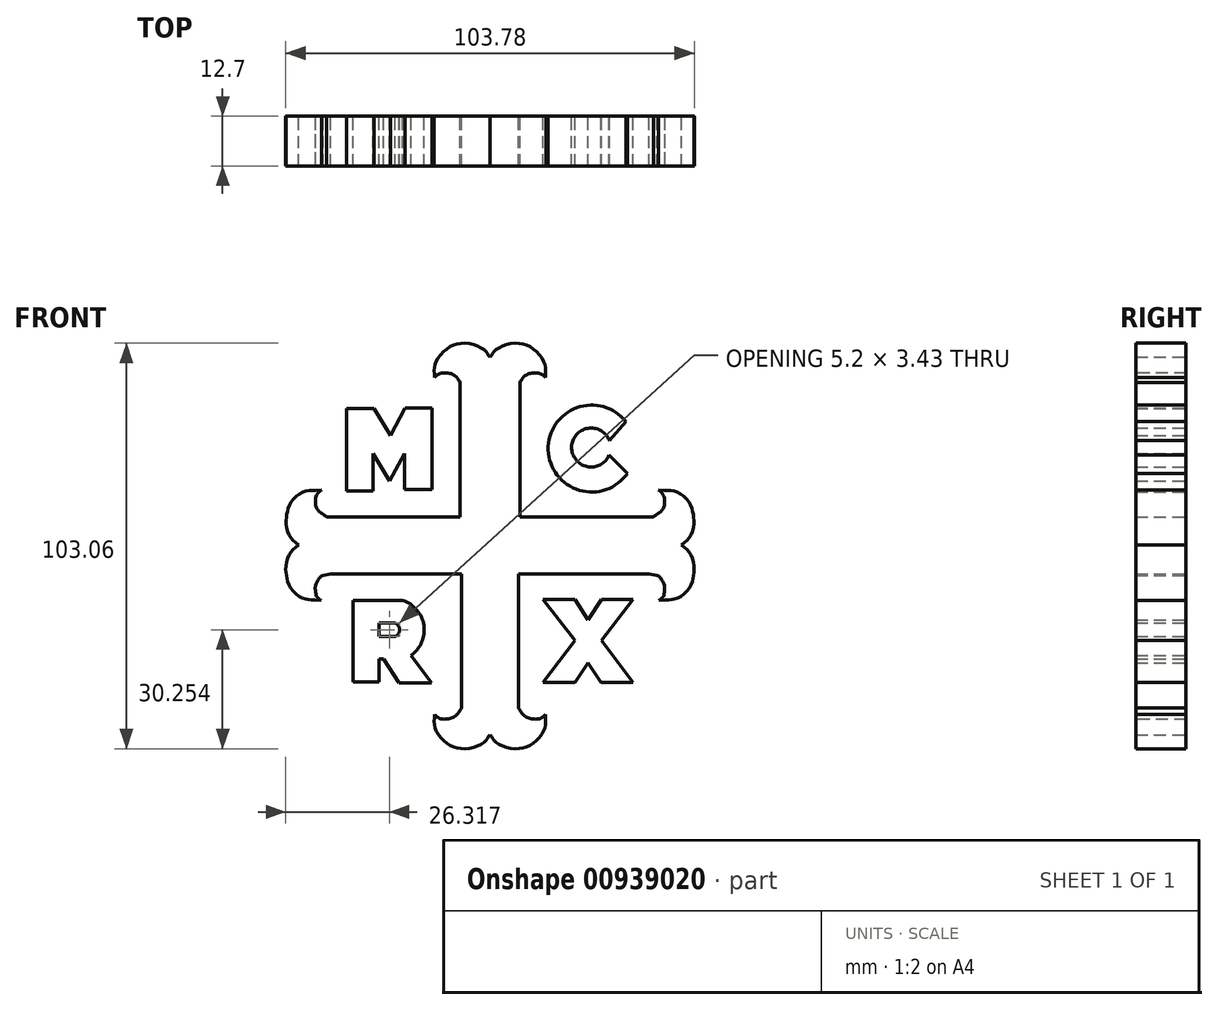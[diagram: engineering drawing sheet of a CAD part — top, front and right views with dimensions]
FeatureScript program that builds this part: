
annotation { "Feature Type Name" : "Feature", "Feature Type Description" : "" }
export const myFeature = defineFeature(function(context is Context, id is Id, definition is map)
    precondition{}
    {
        {
            var Q0;
            Q0=qCreatedBy(makeId("Front.planeOp"),FACE);
            var sketch = newSketch(context, id + "F0", { "sketchPlane" : qUnion([Q0])});
            skFitSpline(sketch, "E0", {"points": [v(0, 47.98) * mm, v(-0.62, 48.8) * mm, v(-1.48, 49.84) * mm, v(-4.4, 51.28) * mm, v(-8.19, 51.36) * mm, v(-10.9, 50.16) * mm, v(-13.4, 47.4) * mm, v(-14.12, 45.3) * mm, v(-14.12, 42.79) * mm], "startDerivative": vector(-12.73, 4.5) * mm, "endDerivative": vector(1.03, -20.51) * mm});
            skFitSpline(sketch, "E1", {"points": [v(-14.12, 42.79) * mm, v(-12.86, 43.77) * mm, v(-11.23, 44) * mm, v(-9.01, 43.33) * mm, v(-7.6, 41.55) * mm], "startDerivative": vector(4.45, 4.62) * mm, "endDerivative": vector(4.3, -7.5) * mm});
            skLineSegment(sketch, "E2", {"start": v(-7.6, 41.55) * mm, "end": v(-7.6, 7.35) * mm});
            skLineSegment(sketch, "E3", {"start": v(-7.6, 7.35) * mm, "end": v(-41.54, 7.35) * mm});
            skFitSpline(sketch, "E4", {"points": [v(-42.78, 14.2) * mm, v(-46.24, 14.03) * mm, v(-48.37, 13.26) * mm, v(-50.63, 11) * mm, v(-51.46, 8.87) * mm, v(-51.78, 6.99) * mm, v(-51.62, 4.41) * mm, v(-50.37, 1.8) * mm, v(-48.69, 0.24) * mm], "startDerivative": vector(-42.61, -0.93) * mm, "endDerivative": vector(18.28, -15.48) * mm});
            skFitSpline(sketch, "E5", {"points": [v(-41.54, 7.35) * mm, v(-43.19, 8.6) * mm, v(-44.2, 10.02) * mm, v(-44.33, 11.44) * mm, v(-42.78, 14.2) * mm], "startDerivative": vector(-3.78, 5.2) * mm, "endDerivative": vector(14.31, 8.46) * mm});
            skFitSpline(sketch, "E6.MirrorCS", {"points": [v(-42.38, -7.52) * mm, v(-43.74, -8.83) * mm, v(-44.37, -10.3) * mm, v(-44.25, -12) * mm, v(-42.95, -13.78) * mm], "startDerivative": vector(-10.08, -1.34) * mm, "endDerivative": vector(14.2, -8.63) * mm});
            skFitSpline(sketch, "E7.MirrorCS", {"points": [v(-42.95, -13.78) * mm, v(-46.4, -13.57) * mm, v(-48.52, -12.77) * mm, v(-50.76, -10.5) * mm, v(-51.57, -8.35) * mm, v(-51.86, -6.46) * mm, v(-51.67, -3.89) * mm, v(-50.39, -1.29) * mm, v(-48.69, 0.24) * mm], "startDerivative": vector(-42.6, 1.43) * mm, "endDerivative": vector(18.46, 15.26) * mm});
            skLineSegment(sketch, "E8", {"start": v(-42.38, -7.52) * mm, "end": v(-40.46, -7.07) * mm});
            skLineSegment(sketch, "E9", {"start": v(-40.46, -7.07) * mm, "end": v(-7.21, -7.07) * mm});
            skFitSpline(sketch, "E10.MirrorCS", {"points": [v(-14.12, -42.79) * mm, v(-12.86, -43.77) * mm, v(-11.23, -44) * mm, v(-9.01, -43.33) * mm, v(-7.18, -41.11) * mm], "startDerivative": vector(4.45, -4.62) * mm, "endDerivative": vector(4.3, 7.5) * mm});
            skFitSpline(sketch, "E11.MirrorCS", {"points": [v(0, -47.98) * mm, v(-0.62, -48.8) * mm, v(-1.48, -49.84) * mm, v(-4.4, -51.28) * mm, v(-8.19, -51.36) * mm, v(-10.9, -50.16) * mm, v(-13.4, -47.4) * mm, v(-14.12, -45.3) * mm, v(-14.12, -42.79) * mm], "startDerivative": vector(-12.73, -4.5) * mm, "endDerivative": vector(1.03, 20.51) * mm});
            skLineSegment(sketch, "E12.MirrorCS", {"start": v(-7.18, -41.11) * mm, "end": v(-7.21, -7.07) * mm});
            skLineSegment(sketch, "E13.MirrorCS", {"start": v(42.38, -7.52) * mm, "end": v(40.46, -7.07) * mm});
            skFitSpline(sketch, "E14.MirrorCS", {"points": [v(42.38, -7.52) * mm, v(43.74, -8.83) * mm, v(44.37, -10.3) * mm, v(44.25, -12) * mm, v(42.95, -13.78) * mm], "startDerivative": vector(10.08, -1.34) * mm, "endDerivative": vector(-14.2, -8.63) * mm});
            skFitSpline(sketch, "E15.MirrorCS", {"points": [v(14.12, 42.79) * mm, v(12.86, 43.77) * mm, v(11.23, 44) * mm, v(9.01, 43.33) * mm, v(7.6, 41.55) * mm], "startDerivative": vector(-4.45, 4.62) * mm, "endDerivative": vector(-4.3, -7.5) * mm});
            skFitSpline(sketch, "E16.MirrorCS", {"points": [v(14.12, -42.79) * mm, v(12.86, -43.77) * mm, v(11.23, -44) * mm, v(9.01, -43.33) * mm, v(7.18, -41.11) * mm], "startDerivative": vector(-4.45, -4.62) * mm, "endDerivative": vector(-4.3, 7.5) * mm});
            skFitSpline(sketch, "E17.MirrorCS", {"points": [v(41.54, 7.35) * mm, v(43.19, 8.6) * mm, v(44.2, 10.02) * mm, v(44.33, 11.44) * mm, v(42.78, 14.2) * mm], "startDerivative": vector(3.78, 5.2) * mm, "endDerivative": vector(-14.31, 8.46) * mm});
            skFitSpline(sketch, "E18.MirrorCS", {"points": [v(0, 47.98) * mm, v(0.62, 48.8) * mm, v(1.48, 49.84) * mm, v(4.4, 51.28) * mm, v(8.19, 51.36) * mm, v(10.9, 50.16) * mm, v(13.4, 47.4) * mm, v(14.12, 45.3) * mm, v(14.12, 42.79) * mm], "startDerivative": vector(12.73, 4.5) * mm, "endDerivative": vector(-1.03, -20.51) * mm});
            skFitSpline(sketch, "E19.MirrorCS", {"points": [v(42.95, -13.78) * mm, v(46.4, -13.57) * mm, v(48.52, -12.77) * mm, v(50.76, -10.5) * mm, v(51.57, -8.35) * mm, v(51.86, -6.46) * mm, v(51.67, -3.89) * mm, v(50.39, -1.29) * mm, v(48.69, 0.24) * mm], "startDerivative": vector(42.6, 1.43) * mm, "endDerivative": vector(-18.46, 15.26) * mm});
            skFitSpline(sketch, "E20.MirrorCS", {"points": [v(0, -47.98) * mm, v(0.62, -48.8) * mm, v(1.48, -49.84) * mm, v(4.4, -51.28) * mm, v(8.19, -51.36) * mm, v(10.9, -50.16) * mm, v(13.4, -47.4) * mm, v(14.12, -45.3) * mm, v(14.12, -42.79) * mm], "startDerivative": vector(12.73, -4.5) * mm, "endDerivative": vector(-1.03, 20.51) * mm});
            skFitSpline(sketch, "E21.MirrorCS", {"points": [v(42.78, 14.2) * mm, v(46.24, 14.03) * mm, v(48.37, 13.26) * mm, v(50.63, 11) * mm, v(51.46, 8.87) * mm, v(51.78, 6.99) * mm, v(51.62, 4.41) * mm, v(50.37, 1.8) * mm, v(48.69, 0.24) * mm], "startDerivative": vector(42.61, -0.93) * mm, "endDerivative": vector(-18.28, -15.48) * mm});
            skLineSegment(sketch, "E22.MirrorCS", {"start": v(7.6, 7.35) * mm, "end": v(41.54, 7.35) * mm});
            skLineSegment(sketch, "E23.MirrorCS", {"start": v(7.18, -41.11) * mm, "end": v(7.21, -7.07) * mm});
            skLineSegment(sketch, "E24.MirrorCS", {"start": v(40.46, -7.07) * mm, "end": v(7.21, -7.07) * mm});
            skLineSegment(sketch, "E25.MirrorCS", {"start": v(7.6, 41.55) * mm, "end": v(7.6, 7.35) * mm});
            skLineSegment(sketch, "E26", {"start": v(-36.42, 14.03) * mm, "end": v(-36.42, 34.9) * mm});
            skLineSegment(sketch, "E27", {"start": v(-36.42, 34.9) * mm, "end": v(-29.46, 34.9) * mm});
            skLineSegment(sketch, "E28", {"start": v(-29.46, 34.9) * mm, "end": v(-25.27, 28.13) * mm});
            skLineSegment(sketch, "E29", {"start": v(-25.27, 28.13) * mm, "end": v(-21.56, 35.08) * mm});
            skLineSegment(sketch, "E30", {"start": v(-21.56, 35.08) * mm, "end": v(-14.7, 35.08) * mm});
            skLineSegment(sketch, "E31", {"start": v(-14.7, 35.08) * mm, "end": v(-14.7, 14.41) * mm});
            skLineSegment(sketch, "E32", {"start": v(-14.7, 14.41) * mm, "end": v(-21.75, 14.41) * mm});
            skLineSegment(sketch, "E33", {"start": v(-21.75, 14.41) * mm, "end": v(-21.75, 23.46) * mm});
            skLineSegment(sketch, "E34", {"start": v(-21.75, 23.46) * mm, "end": v(-25.46, 16.5) * mm});
            skLineSegment(sketch, "E35", {"start": v(-25.46, 16.5) * mm, "end": v(-29.75, 23.56) * mm});
            skLineSegment(sketch, "E36", {"start": v(-29.75, 23.56) * mm, "end": v(-29.75, 14.03) * mm});
            skLineSegment(sketch, "E37", {"start": v(-29.75, 14.03) * mm, "end": v(-36.42, 14.03) * mm});
            skLineSegment(sketch, "E38", {"start": v(30.32, 26.8) * mm, "end": v(34.53, 31.58) * mm});
            skLineSegment(sketch, "E39", {"start": v(30.24, 23.1) * mm, "end": v(34.93, 18.49) * mm});
            skArc(sketch, "E40", {"start": v(30.32, 26.8) * mm, "mid": v(20.73, 25.14) * mm, "end": v(30.24, 23.1) * mm});
            skArc(sketch, "E41", {"start": v(34.53, 31.58) * mm, "mid": v(14.79, 24.43) * mm, "end": v(34.93, 18.49) * mm});
            skLineSegment(sketch, "E42", {"start": v(-34.86, -34.5) * mm, "end": v(-28.13, -34.5) * mm});
            skLineSegment(sketch, "E43", {"start": v(-28.13, -34.5) * mm, "end": v(-28.13, -28.65) * mm});
            skLineSegment(sketch, "E44", {"start": v(-28.13, -28.65) * mm, "end": v(-27, -28.65) * mm});
            skLineSegment(sketch, "E45", {"start": v(-27, -28.65) * mm, "end": v(-23.16, -34.74) * mm});
            skLineSegment(sketch, "E46", {"start": v(-23.16, -34.74) * mm, "end": v(-14.83, -34.74) * mm});
            skLineSegment(sketch, "E47", {"start": v(-14.83, -34.74) * mm, "end": v(-20.04, -27.77) * mm});
            skLineSegment(sketch, "E48", {"start": v(-34.86, -34.5) * mm, "end": v(-34.86, -13.83) * mm});
            skLineSegment(sketch, "E49", {"start": v(-34.86, -13.83) * mm, "end": v(-22.2, -13.83) * mm});
            skArc(sketch, "E50", {"start": v(-20.04, -27.77) * mm, "mid": v(-16.8, -20.13) * mm, "end": v(-22.2, -13.83) * mm});
            skLineSegment(sketch, "E51", {"start": v(-24.12, -23) * mm, "end": v(-28.17, -23) * mm});
            skLineSegment(sketch, "E52", {"start": v(-28.17, -23) * mm, "end": v(-28.17, -19.56) * mm});
            skLineSegment(sketch, "E53", {"start": v(-28.17, -19.56) * mm, "end": v(-24.12, -19.56) * mm});
            skArc(sketch, "E54", {"start": v(-24.12, -23) * mm, "mid": v(-22.97, -21.28) * mm, "end": v(-24.12, -19.56) * mm});
            skLineSegment(sketch, "E55", {"start": v(21.53, -13.55) * mm, "end": v(24.9, -18.83) * mm});
            skLineSegment(sketch, "E56", {"start": v(21.53, -13.55) * mm, "end": v(13.52, -13.55) * mm});
            skLineSegment(sketch, "E57", {"start": v(13.52, -13.55) * mm, "end": v(21.53, -23.96) * mm});
            skLineSegment(sketch, "E58", {"start": v(21.53, -23.96) * mm, "end": v(13.52, -34.7) * mm});
            skLineSegment(sketch, "E59", {"start": v(13.52, -34.7) * mm, "end": v(21.64, -34.7) * mm});
            skLineSegment(sketch, "E60", {"start": v(21.64, -34.7) * mm, "end": v(24.9, -29.75) * mm});
            skLineSegment(sketch, "E61.MirrorCS", {"start": v(36.27, -13.55) * mm, "end": v(28.26, -23.96) * mm});
            skLineSegment(sketch, "E62.MirrorCS", {"start": v(28.26, -13.55) * mm, "end": v(24.9, -18.83) * mm});
            skLineSegment(sketch, "E63.MirrorCS", {"start": v(28.26, -13.55) * mm, "end": v(36.27, -13.55) * mm});
            skLineSegment(sketch, "E64.MirrorCS", {"start": v(28.26, -23.96) * mm, "end": v(36.27, -34.7) * mm});
            skLineSegment(sketch, "E65.MirrorCS", {"start": v(28.16, -34.7) * mm, "end": v(24.9, -29.75) * mm});
            skLineSegment(sketch, "E66.MirrorCS", {"start": v(36.27, -34.7) * mm, "end": v(28.16, -34.7) * mm});
            skSolve(sketch);
        }
        {
            var Q0;
            Q0 = qSketchRegion(id + "F0", true);
            extrude(context, id + "F1", {"entities" : qUnion([Q0]), "depth" : 12.7 * mm, "offsetDistance" : 25.4 * mm});
        }
    });
